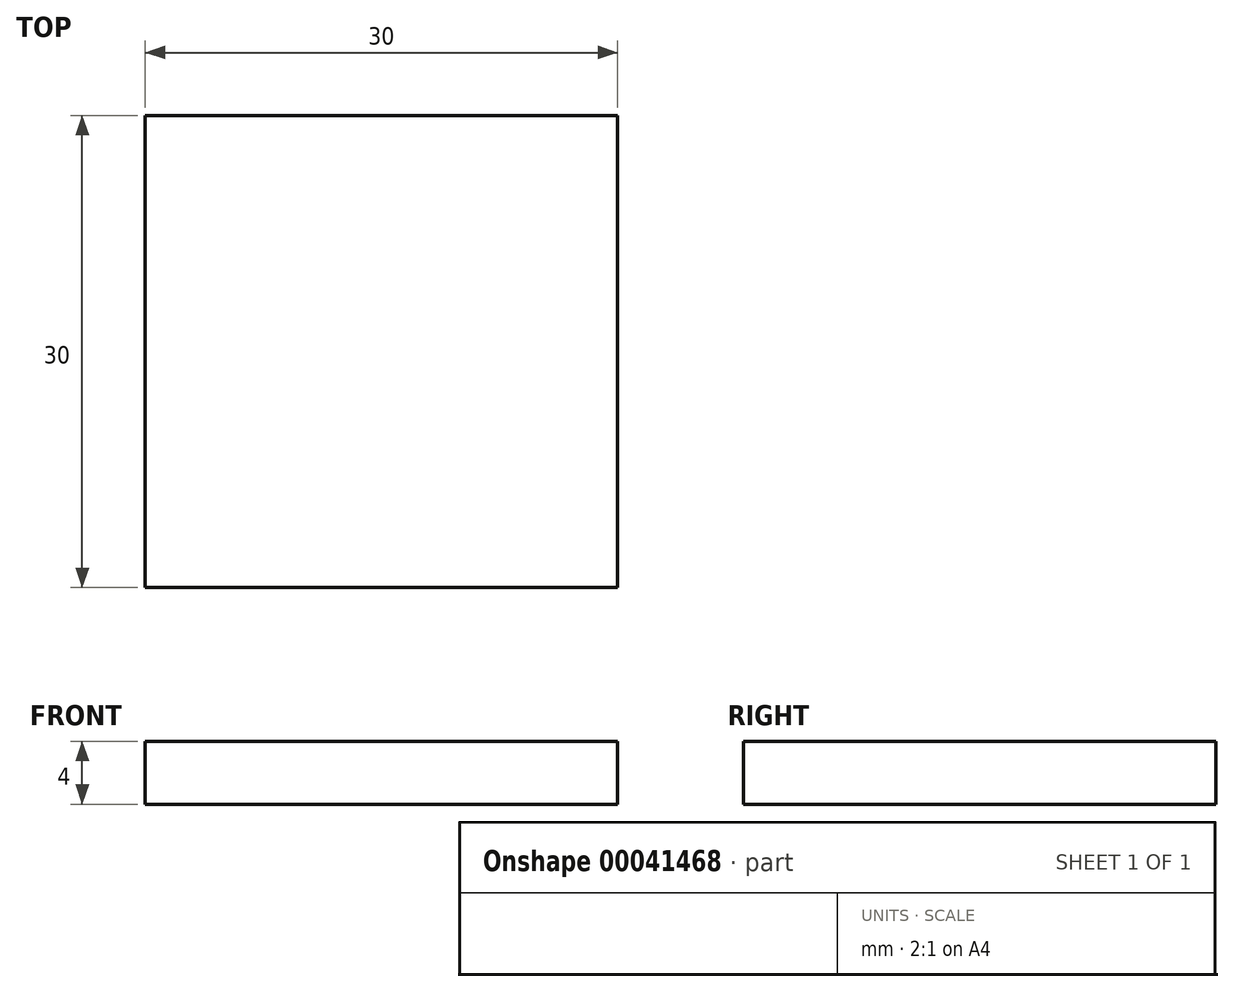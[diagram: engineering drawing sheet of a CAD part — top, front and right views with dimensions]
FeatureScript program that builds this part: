
annotation { "Feature Type Name" : "Feature", "Feature Type Description" : "" }
export const myFeature = defineFeature(function(context is Context, id is Id, definition is map)
    precondition{}
    {
        {
            var Q0;
            Q0=qCreatedBy(makeId("Top.planeOp"),FACE);
            var sketch = newSketch(context, id + "F0", { "sketchPlane" : qUnion([Q0])});
            skLineSegment(sketch, "E0.rect.bottom", {"start": v(15, 15) * mm, "end": v(-15, 15) * mm});
            skLineSegment(sketch, "E0.rect.top", {"start": v(15, -15) * mm, "end": v(-15, -15) * mm});
            skLineSegment(sketch, "E0.rect.left", {"start": v(15, 15) * mm, "end": v(15, -15) * mm});
            skLineSegment(sketch, "E0.rect.right", {"start": v(-15, 15) * mm, "end": v(-15, -15) * mm});
            skPoint(sketch, "E0.rect.middle", {"position": v(0, 0) * mm});
            skSolve(sketch);
        }
        {
            var Q0;
            Q0 = qSketchRegion(id + "F0", true);
            extrude(context, id + "F1", {"entities" : qUnion([Q0]), "depth" : 4 * mm});
        }
    });
